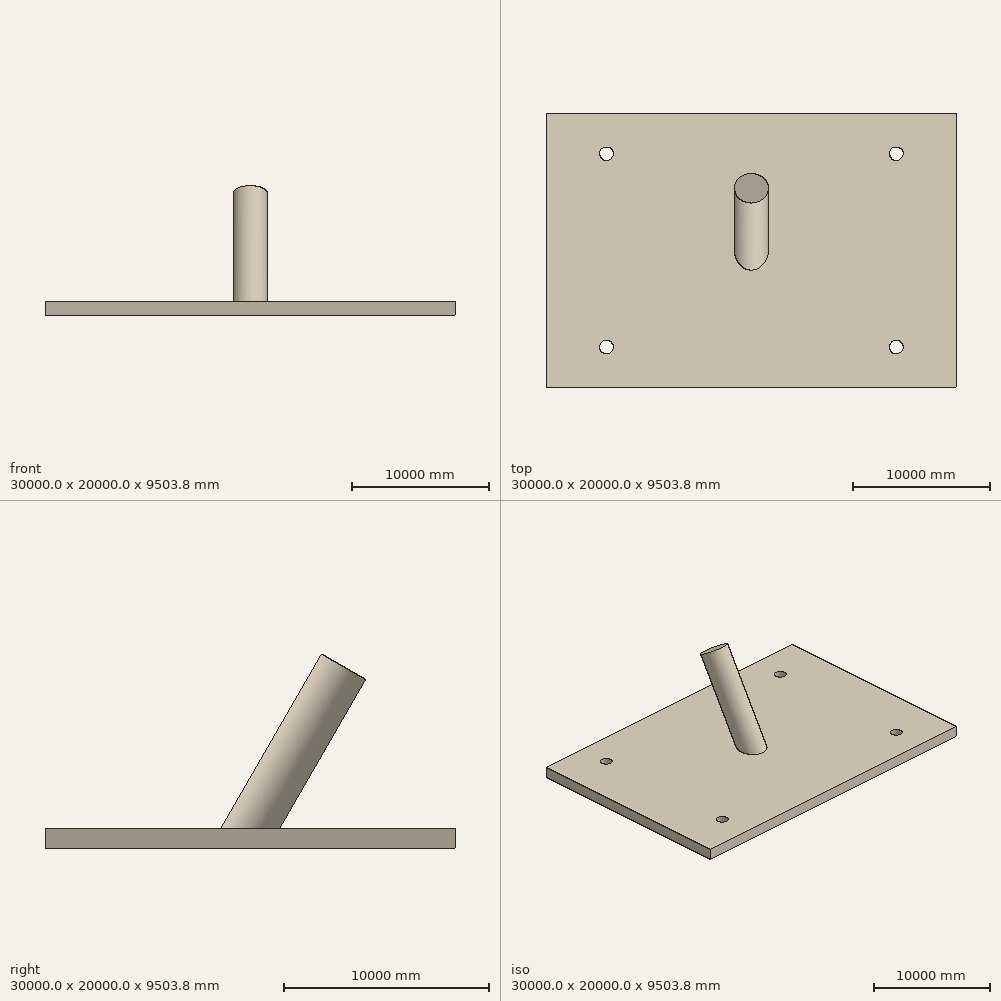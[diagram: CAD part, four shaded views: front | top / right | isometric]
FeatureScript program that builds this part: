
annotation { "Feature Type Name" : "Feature", "Feature Type Description" : "" }
export const myFeature = defineFeature(function(context is Context, id is Id, definition is map)
    precondition{}
    {
        {
            var Q0;
            Q0=qCreatedBy(makeId("Top.planeOp"),FACE);
            var sketch = newSketch(context, id + "F0", { "sketchPlane" : qUnion([Q0])});
            skLineSegment(sketch, "E0.bottom", {"start": v(15000, -10000) * mm, "end": v(-15000, -10000) * mm});
            skLineSegment(sketch, "E0.top", {"start": v(14995, 10000) * mm, "end": v(-14995, 10000) * mm});
            skLineSegment(sketch, "E0.left", {"start": v(15000, -10000) * mm, "end": v(15000, 9995) * mm});
            skLineSegment(sketch, "E0.right", {"start": v(-15000, -10000) * mm, "end": v(-15000, 9995) * mm});
            skLineSegment(sketch, "E1", {"start": v(-15000, 10000) * mm, "end": v(15000, -10000) * mm, "construction": true});
            skLineSegment(sketch, "E2", {"start": v(15000, 10000) * mm, "end": v(-15000, -10000) * mm, "construction": true});
            skPoint(sketch, "E3", {"position": v(0, 0) * mm});
            skEllipse(sketch, "E4", {"center": v(0, 0) * mm, "majorRadius": 2500 * mm, "minorRadius": 500 * mm, "majorAxis": v(0, 1), "construction": true});
            skPoint(sketch, "E5", {"position": v(-10606.6, 7071.07) * mm});
            skPoint(sketch, "E6", {"position": v(10606.6, 7071.07) * mm});
            skPoint(sketch, "E7", {"position": v(10606.6, -7071.07) * mm});
            skPoint(sketch, "E8", {"position": v(-10606.6, -7071.07) * mm});
            skCircle(sketch, "E9", {"center": v(-10606.6, 7071.07) * mm, "radius": 500 * mm});
            skCircle(sketch, "E10", {"center": v(10606.6, 7071.07) * mm, "radius": 500 * mm});
            skCircle(sketch, "E11", {"center": v(-10606.6, -7071.07) * mm, "radius": 500 * mm});
            skCircle(sketch, "E12", {"center": v(10606.6, -7071.07) * mm, "radius": 500 * mm});
            skPoint(sketch, "E13.visualSharp", {"position": v(-15000, 10000) * mm});
            skArc(sketch, "E13.filletArc", {"start": v(-14995, 10000) * mm, "mid": v(-14998.54, 9998.54) * mm, "end": v(-15000, 9995) * mm});
            skPoint(sketch, "E14.visualSharp", {"position": v(15000, 10000) * mm});
            skArc(sketch, "E14.filletArc", {"start": v(15000, 9995) * mm, "mid": v(14998.54, 9998.54) * mm, "end": v(14995, 10000) * mm});
            skSolve(sketch);
        }
        {
            var Q0;
            Q0=makeQuery(id+"F0.imprint","IMPRINT",FACE,{"disambiguationData":[TD([[makeQuery(id+"F0.imprint","IMPRINT",EDGE,{"derivedFrom":sQuery(id+"F0.wireOp",EDGE,"E0.bottom")}),-1.0]])]});
            var Q1;
            Q1=sQuery(id+"F0.wireOp",EDGE,"E0.top");
            var Q2;
            Q2=sQuery(id+"F0.wireOp",EDGE,"E0.right");
            var Q3;
            Q3=sQuery(id+"F0.wireOp",EDGE,"E0.left");
            var Q4;
            Q4=sQuery(id+"F0.wireOp",EDGE,"E0.bottom");
            extrude(context, id + "F1", {"entities" : qUnion([Q0]), "surfaceEntities" : qUnion([Q1, Q2, Q3, Q4]), "oppositeDirection" : true, "depth" : 1000 * mm});
        }
        {
            var Q0;
            Q0=makeQuery(id+"F1.opExtrude","CAP_EDGE",EDGE,{"disambiguationData":[OSD([sQuery(id+"F0.wireOp",EDGE,"E0.top")])],"isStart":true});
            var Q1;
            Q1=qCreatedBy(makeId("Origin.pointOp"),VERTEX);
            cPlane(context, id + "F2", {"entities" : qUnion([Q0, Q1]), "cplaneType" : CPlaneType.LINE_ANGLE, "offset" : 25 * mm, "angle" : 30 * degree, "width" : 150 * mm, "height" : 150 * mm});
        }
        {
            var Q0;
            Q0=qCreatedBy(id+"F2.planeOp",FACE);
            var sketch = newSketch(context, id + "F3", { "sketchPlane" : qUnion([Q0])});
            skCircle(sketch, "E15", {"center": v(0, 0) * mm, "radius": 1245.92 * mm});
            skSolve(sketch);
        }
        {
            var Q0;
            Q0 = qSketchRegion(id + "F3", true);
            var Q1;
            Q1=makeQuery(id+"F1.opExtrude","SWEPT_BODY",BODY,{"disambiguationData":[OSD([sQuery(id+"F0.wireOp",EDGE,"E0.bottom"),sQuery(id+"F0.wireOp",EDGE,"E0.top"),sQuery(id+"F0.wireOp",EDGE,"E0.left"),sQuery(id+"F0.wireOp",EDGE,"E0.right"),sQuery(id+"F0.wireOp",EDGE,"E9"),sQuery(id+"F0.wireOp",EDGE,"E10"),sQuery(id+"F0.wireOp",EDGE,"E11"),sQuery(id+"F0.wireOp",EDGE,"E12"),sQuery(id+"F0.wireOp",EDGE,"E13.filletArc"),sQuery(id+"F0.wireOp",EDGE,"E14.filletArc")])]});
            extrude(context, id + "F4", {"entities" : qUnion([Q0]), "operationType" : NewBodyOperationType.ADD, "endBound" : BoundingType.UP_TO_NEXT, "oppositeDirection" : true, "endBoundEntityBody" : qUnion([Q1]), "depth" : 300 * mm, "hasSecondDirection" : true, "secondDirectionOppositeDirection" : false, "secondDirectionDepth" : 4100 * mm});
        }
    });
